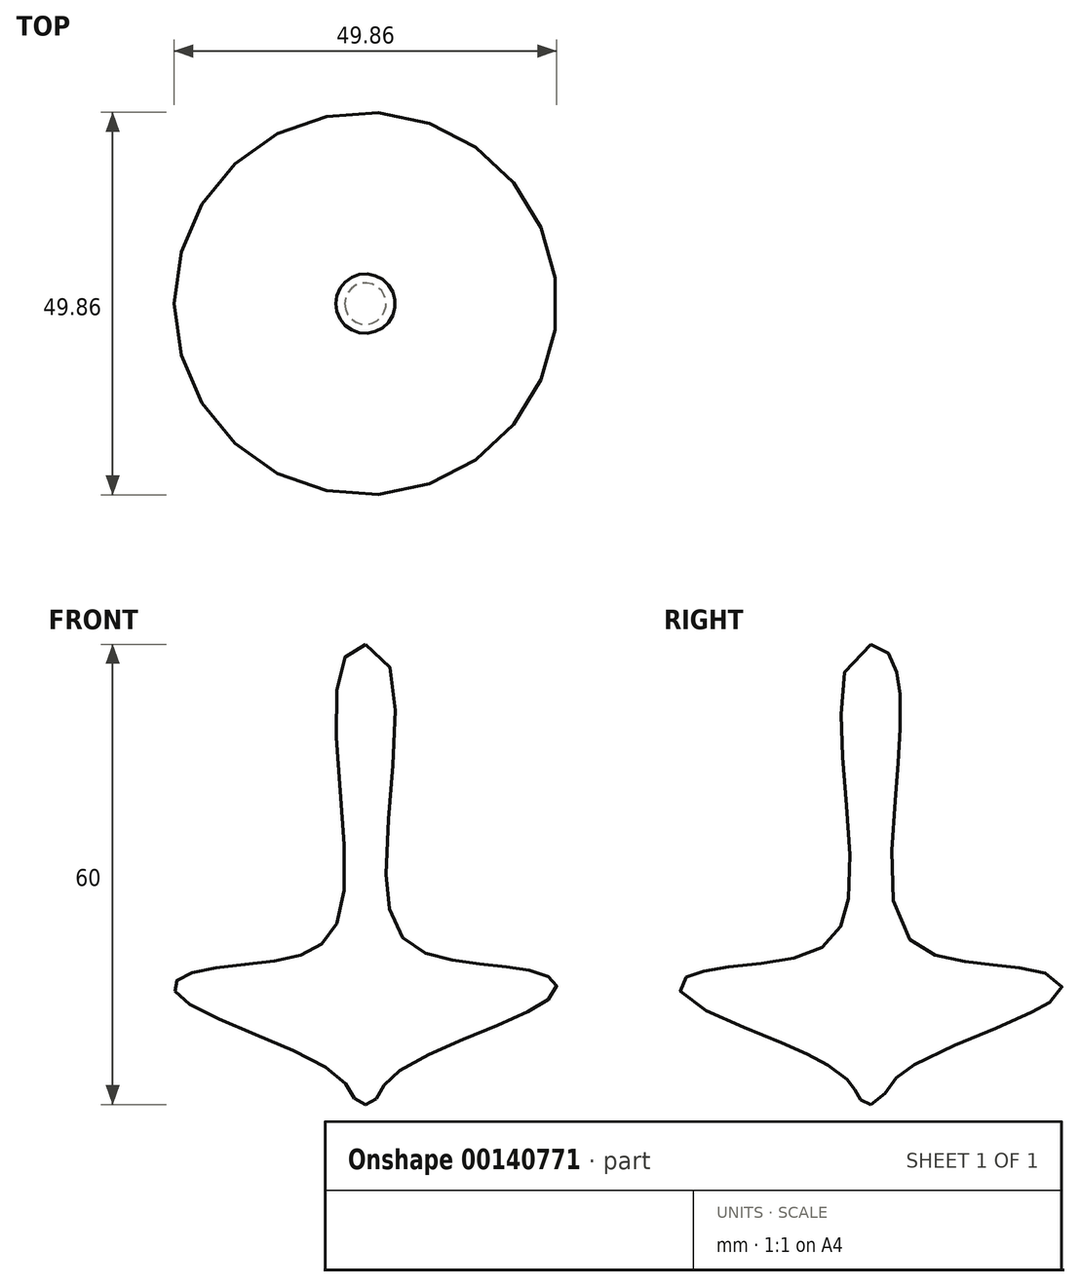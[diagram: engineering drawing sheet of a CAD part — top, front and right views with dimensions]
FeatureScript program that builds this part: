
annotation { "Feature Type Name" : "Feature", "Feature Type Description" : "" }
export const myFeature = defineFeature(function(context is Context, id is Id, definition is map)
    precondition{}
    {
        {
            var Q0;
            Q0=qCreatedBy(makeId("Front.planeOp"),FACE);
            var sketch = newSketch(context, id + "F0", { "sketchPlane" : qUnion([Q0])});
            skLineSegment(sketch, "E0", {"start": v(0, 0) * mm, "end": v(0, 60) * mm});
            skLineSegment(sketch, "E1", {"start": v(0, 60) * mm, "end": v(-25, 60) * mm, "construction": true});
            skLineSegment(sketch, "E2", {"start": v(0, 0) * mm, "end": v(-25, 0) * mm, "construction": true});
            skLineSegment(sketch, "E3", {"start": v(-25, 60) * mm, "end": v(-25, 0) * mm, "construction": true});
            skFitSpline(sketch, "E4", {"points": [v(0, 60) * mm, v(-2.88, 26.88) * mm, v(-11.48, 18.79) * mm, v(-24.23, 16.47) * mm, v(-24.21, 14) * mm, v(-3.25, 3.42) * mm, v(0, 0) * mm], "startDerivative": vector(-83.14, 0) * mm, "endDerivative": vector(51.7, 0) * mm});
            skLineSegment(sketch, "E5", {"start": v(-4, 60) * mm, "end": v(-4, 0) * mm, "construction": true});
            skLineSegment(sketch, "E6", {"start": v(0, 0) * mm, "end": v(-25, 11.66) * mm, "construction": true});
            skSolve(sketch);
        }
        {
            var Q0;
            Q0=makeQuery(id+"F0.imprint","IMPRINT",FACE,{"disambiguationData":[TD([[makeQuery(id+"F0.imprint","IMPRINT",EDGE,{"derivedFrom":sQuery(id+"F0.wireOp",EDGE,"E0")}),1.0]])]});
            var Q1;
            Q1=sQuery(id+"F0.wireOp",EDGE,"E0");
            revolve(context, id + "F1", {"entities" : qUnion([Q0]), "axis" : qUnion([Q1]), "revolveType" : RevolveType.FULL});
        }
    });
